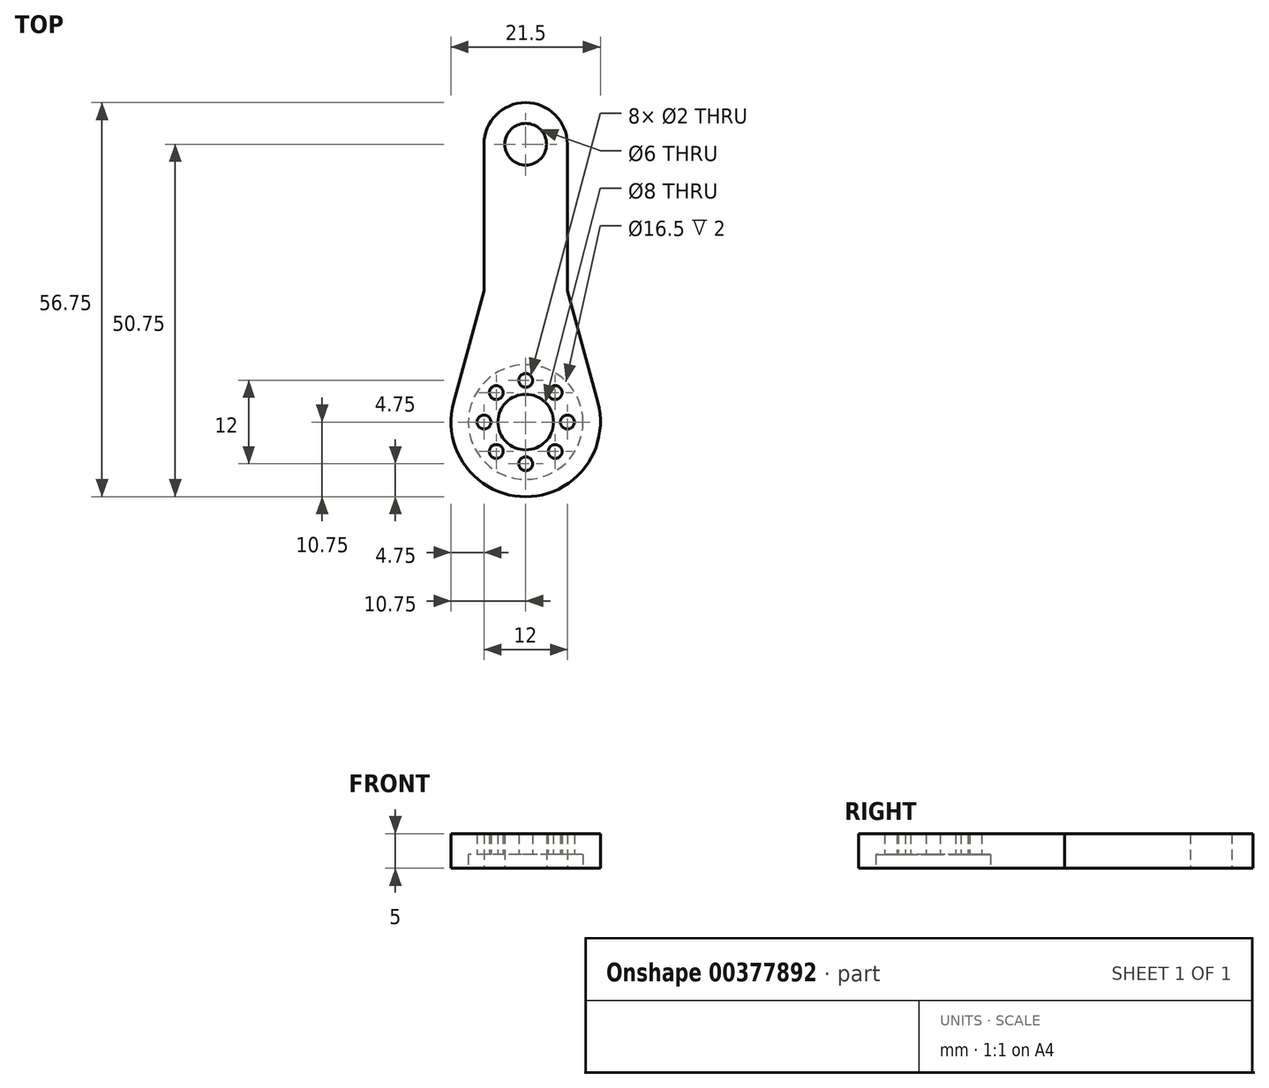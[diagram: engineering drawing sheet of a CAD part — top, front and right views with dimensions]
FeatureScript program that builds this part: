
annotation { "Feature Type Name" : "Feature", "Feature Type Description" : "" }
export const myFeature = defineFeature(function(context is Context, id is Id, definition is map)
    precondition{}
    {
        {
            var Q0;
            Q0=qCreatedBy(makeId("Top.planeOp"),FACE);
            var sketch = newSketch(context, id + "F0", { "sketchPlane" : qUnion([Q0])});
            skCircle(sketch, "E0", {"center": v(0, 0) * mm, "radius": 8.25 * mm});
            skCircle(sketch, "E1", {"center": v(0, 0) * mm, "radius": 4 * mm});
            skCircle(sketch, "E2", {"center": v(6, 0) * mm, "radius": 1 * mm});
            skArc(sketch, "E3", {"start": v(-6, 8.92) * mm, "mid": v(0, -10.75) * mm, "end": v(6, 8.92) * mm});
            skPoint(sketch, "E4", {"position": v(8.25, 0) * mm});
            skPoint(sketch, "E5", {"position": v(10.75, 0) * mm});
            skLineSegment(sketch, "E6", {"start": v(10.75, 0) * mm, "end": v(10.75, 40) * mm});
            skArc(sketch, "E7", {"start": v(6, 40) * mm, "mid": v(0, 46) * mm, "end": v(-6, 40) * mm});
            skCircle(sketch, "E8.1.0", {"center": v(4.24, 4.24) * mm, "radius": 1 * mm});
            skCircle(sketch, "E8.2.0", {"center": v(0, 6) * mm, "radius": 1 * mm});
            skCircle(sketch, "E8.3.0", {"center": v(-4.24, 4.24) * mm, "radius": 1 * mm});
            skCircle(sketch, "E8.4.0", {"center": v(-6, 0) * mm, "radius": 1 * mm});
            skCircle(sketch, "E8.5.0", {"center": v(-4.24, -4.24) * mm, "radius": 1 * mm});
            skCircle(sketch, "E8.6.0", {"center": v(0, -6) * mm, "radius": 1 * mm});
            skCircle(sketch, "E8.7.0", {"center": v(4.24, -4.24) * mm, "radius": 1 * mm});
            skArc(sketch, "E9", {"start": v(10.75, 40) * mm, "mid": v(0, 50.75) * mm, "end": v(-10.75, 40) * mm});
            skLineSegment(sketch, "E10.MirrorCS", {"start": v(-10.75, 0) * mm, "end": v(-10.75, 40) * mm});
            skCircle(sketch, "E11", {"center": v(0, 40) * mm, "radius": 3 * mm});
            skLineSegment(sketch, "E12", {"start": v(6, 40) * mm, "end": v(6, 8.92) * mm});
            skLineSegment(sketch, "E13.MirrorCS", {"start": v(-6, 40) * mm, "end": v(-6, 8.92) * mm});
            skLineSegment(sketch, "E14", {"start": v(-6, 18.92) * mm, "end": v(-10.37, 2.82) * mm});
            skLineSegment(sketch, "E15.MirrorCS", {"start": v(6, 18.92) * mm, "end": v(10.37, 2.82) * mm});
            skSolve(sketch);
        }
        {
            var Q0;
            Q0=makeQuery(id+"F0.imprint","IMPRINT",FACE,{"disambiguationData":[TD([[makeQuery(id+"F0.imprint","IMPRINT",EDGE,{"derivedFrom":sQuery(id+"F0.wireOp",EDGE,"E0")}),-1.0]])]});
            var Q1;
            Q1=makeQuery(id+"F0.imprint","IMPRINT",FACE,{"disambiguationData":[TD([[makeQuery(id+"F0.imprint","IMPRINT",EDGE,{"derivedFrom":sQuery(id+"F0.wireOp",EDGE,"E0")}),1.0]])]});
            var Q2;
            {var subQ3=sQuery(id+"F0.wireOp",EDGE,"E14");Q2=makeQuery(id+"F0.imprint","IMPRINT",FACE,{"disambiguationData":[TD([[makeQuery(id+"F0.imprint","IMPRINT",EDGE,{"derivedFrom":subQ3}),1.0]])]});}
            var Q3;
            {var subQ3=sQuery(id+"F0.wireOp",EDGE,"E15.MirrorCS");Q3=makeQuery(id+"F0.imprint","IMPRINT",FACE,{"disambiguationData":[TD([[makeQuery(id+"F0.imprint","IMPRINT",EDGE,{"derivedFrom":subQ3}),-1.0]])]});}
            extrude(context, id + "F1", {"entities" : qUnion([Q0, Q1, Q2, Q3]), "depth" : 5 * mm});
        }
        {
            var Q0;
            Q0=makeQuery(id+"F0.imprint","IMPRINT",FACE,{"disambiguationData":[TD([[makeQuery(id+"F0.imprint","IMPRINT",EDGE,{"derivedFrom":sQuery(id+"F0.wireOp",EDGE,"E0")}),1.0]])]});
            extrude(context, id + "F2", {"entities" : qUnion([Q0]), "operationType" : NewBodyOperationType.REMOVE, "depth" : 2 * mm});
        }
    });
